# Revit family: IS_ConnectSpace_E0362_BIM_DE
name_source: partatom
category: Plumbing Fixtures
revit_build: Autodesk Revit MEP 2016 (Build: 20161004_0715(x64)
units: mm (PartAtom-declared; Revit-internal decimal feet)

## family parameters
Always vertical = No
Cut with Voids When Loaded = No
OmniClass Number = 23.45.05.14.21.11
OmniClass Title = Bath/Shower Units
Part Type = Normal
Room Calculation Point = No
Round Connector Dimension = Use Diameter
Shared = No
Work Plane-Based = No

## types (3) — shared parameters
Accessories = www.idealstandard.de\ersatzteile
AssetType = Fixed
BIMobject category = Storage
BOSUseNativeGeometries = 1
Brand = Ideal Standard
Brand url = http://www.idealstandard.de
CodePerformance = 0
ConnectionType = Plumbing
CurrencyUnit = €
CurrentRevision = 1
DurationUnit = Jaar
EAN code = https://5017830454922
Edition number = 1
ExpectedLife = 25
Features = CONNECT SPACE glass shelf 218x232mm
IFC Classification = Sanitary Terminal
IfcExportAs = Sanitary terminal type
IfcExportType = FURNITURE
Installation instructions = http://www.idealstandard.de
InstallationInstructions = www.idealstandard.de\produkte
LinearUnits = millimetres
MaintenanceInformation = www.idealstandard.de
Manufacturer = http://www.idealstandard.de
Manufacturer name = Ideal Standard
ManufacturerURL = http://www.idealstandard.de
Material = glass
Material main = Glass
NettWeight = 0,755 kg
Nominal height = 6
Nominal width = 218
NominalHeight = 6 mm  [stored 0.019685 ft]
NominalLength = 218 mm  [stored 0.715223 ft]
NominalWidth = 232 mm  [stored 0.761155 ft]
Product Guid = 317f02ba-d95e-46a4-8287-eb2cc187e43b
Product SKU = E0362
Product certification = 0
Product data url = https://bimobject.com
Product family = CONNECT SPACE
Product group = Furniture
Product name = CONNECT SPACE glass shelf 218x232mm
Product url = http://www.idealstandard.de
ProductInformation = www.idealstandard.de/produkte
QR code = http://bimobject.com
Shape = Rectangular
Size = 232x118x6 mm
Space = Internal
SpareParts = www.idealstandard.de/ersatzteile
Technical description = http://www.idealstandard.de
URL = http://www.idealstandard.de
Uniclass2015Code = Pr_40_30_78_03
Uniclass2015Title = Bathroom cabinets
Uniclass2015Version = Products v1.1
VolumeUnits = Litres
Weight Net (Kg) = 0.76
zero-valued in all types: Cost

## per-type parameters (varying)
| type | BIMObjectName | BarCode | Color | Finish | MainColor | Model | ModelNumber | Name |
| E0362RP CONNECT SPACE glass shelf 218x232mm | ISI_IdealStandard_BathroomCabinets_CONNECTSPACE_E0362RP | 5017830454908 | Light Brown Glass | Light Brown Glass | Light Brown Glass | E0362RP | E0362RP | ISI_IdealStandard_BathroomCabinets_CONNECTSPACE_E0362RP |
| E0362RU CONNECT SPACE glass shelf 218x232mm | ISI_IdealStandard_BathroomCabinets_CONNECTSPACE_E0362RU | 5017830454915 | Grey Glass | Grey Glass | Grey Glass | E0362RU | E0362RU | ISI_IdealStandard_BathroomCabinets_CONNECTSPACE_E0362RU |
| E0362SA CONNECT SPACE glass shelf 218x232mm | ISI_IdealStandard_BathroomCabinets_CONNECTSPACE_E0362SA | 5017830454922 | White Glass | White Glass | White Glass | E0362SA | E0362SA | ISI_IdealStandard_BathroomCabinets_CONNECTSPACE_E0362SA |

note: column(s) folded — value = type name in every type: Description, ModelReference

note: [stored X ft] marks values corroborated as IEEE doubles in the binary element streams (Revit-internal decimal feet)

## geometry (parser evidence)
native form markers: Blend x2, Sweep x3
no freeform markers — native parametric forms only
